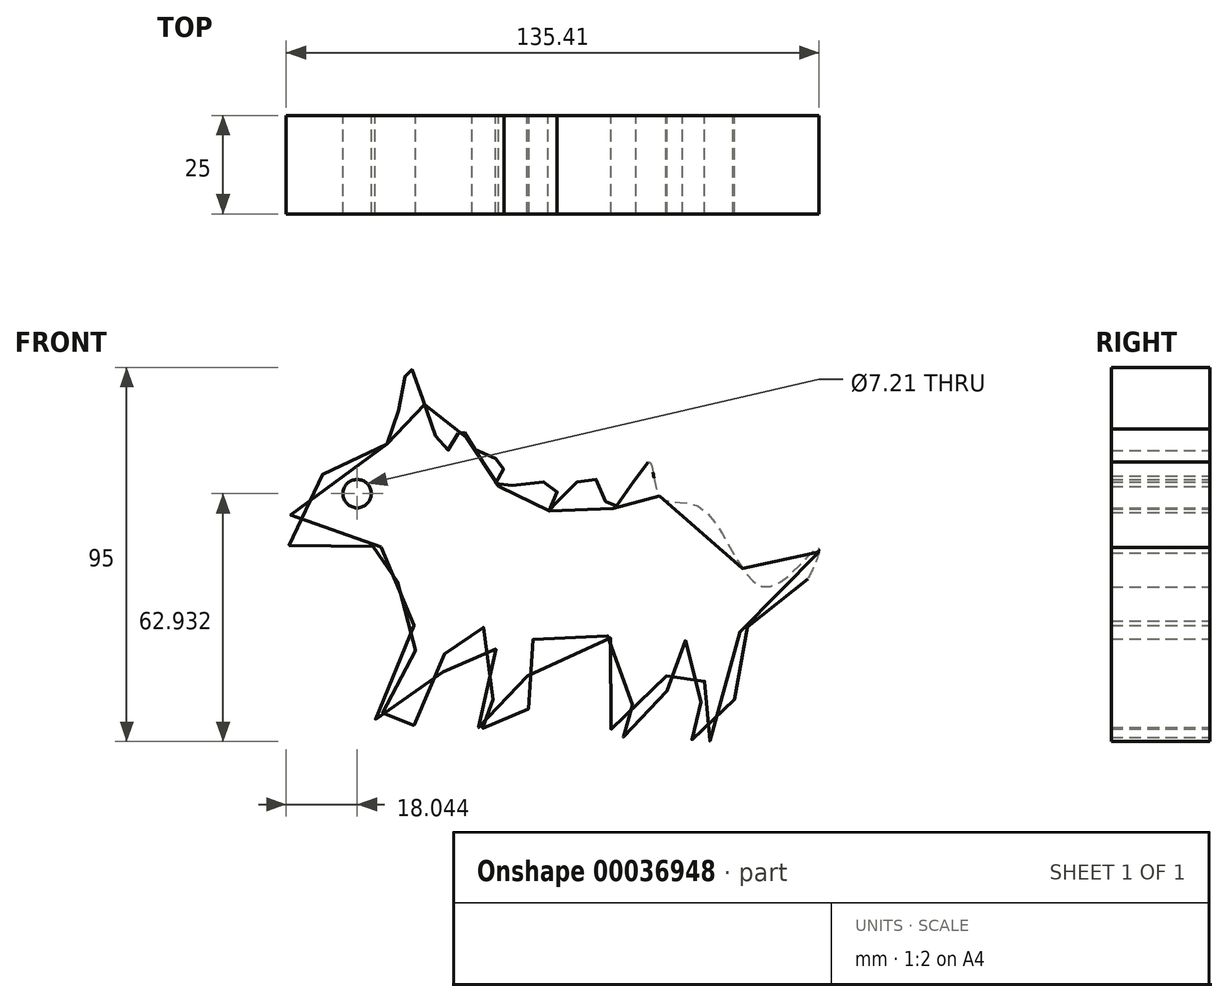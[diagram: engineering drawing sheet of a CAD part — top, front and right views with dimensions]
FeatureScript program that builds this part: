
annotation { "Feature Type Name" : "Feature", "Feature Type Description" : "" }
export const myFeature = defineFeature(function(context is Context, id is Id, definition is map)
    precondition{}
    {
        {
            var Q0;
            Q0=qCreatedBy(makeId("Front.planeOp"),FACE);
            var sketch = newSketch(context, id + "F0", { "sketchPlane" : qUnion([Q0])});
            skFitSpline(sketch, "E0", {"points": [v(-56.91, 26.25) * mm, v(-51.07, 45.66) * mm, v(-42.04, 24.59) * mm, v(-38.18, 30.06) * mm, v(-35.04, 25.24) * mm, v(-27.23, 20.78) * mm, v(-29.22, 15.81) * mm, v(-13.98, 15.65) * mm, v(-16.1, 8.87) * mm, v(-5.08, 18.12) * mm, v(0, 9.82) * mm, v(9.5, 21.65) * mm, v(12.26, 13.01) * mm, v(23.05, 9.91) * mm, v(39.41, -10.08) * mm, v(52.59, 0) * mm, v(44.16, -15.66) * mm, v(31.76, -22.94) * mm, v(29.25, -47.36) * mm, v(18.29, -47.65) * mm, v(21.5, -42.4) * mm, v(21.62, -25.83) * mm, v(14.67, -24.4) * mm, v(12.15, -45.82) * mm, v(0, -46.9) * mm, v(4.97, -40.88) * mm, v(0, -23.1) * mm, v(-19.78, -23.28) * mm, v(-20.97, -40.57) * mm, v(-26.87, -45.88) * mm, v(-35.29, -44.96) * mm, v(-30.67, -39.74) * mm, v(-31.78, -20.93) * mm, v(-40.74, -20.66) * mm, v(-46.13, -43.09) * mm, v(-59.93, -44.35) * mm, v(-54.34, -38.85) * mm, v(-50.2, -19.57) * mm, v(-55.34, -5.4) * mm, v(-57.57, 0) * mm, v(-81.3, 0) * mm, v(-73.22, 18.61) * mm, v(-56.91, 26.25) * mm]});
            skCircle(sketch, "E1", {"center": v(-64.53, 13.66) * mm, "radius": 3.6 * mm});
            skSolve(sketch);
        }
        {
            var Q0;
            Q0 = qSketchRegion(id + "F0", true);
            extrude(context, id + "F1", {"entities" : qUnion([Q0]), "depth" : 25 * mm});
        }
    });
